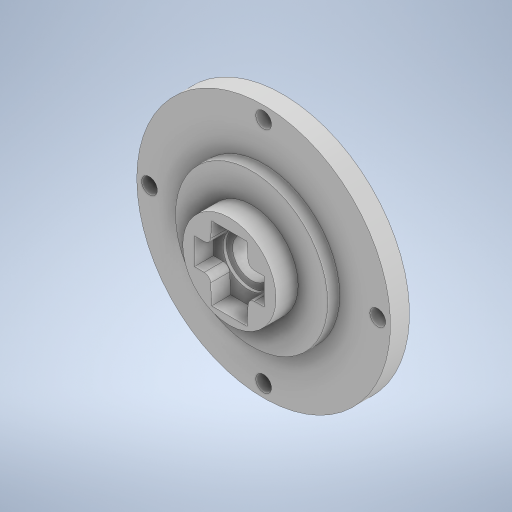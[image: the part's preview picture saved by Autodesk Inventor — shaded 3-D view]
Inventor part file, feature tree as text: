
AUTODESK INVENTOR PART (.ipt)
format: ipt  version: 2023.1 (Build 271208000, 208)  size: 600,576 bytes
history: native  units: mm
features: sketch x18, extrude x18, projected_geometry x7, fillet x2, other x1
ambient origin geometry x8: Origin, YZ Plane, XZ Plane, XY Plane, X Axis, Y Axis, Z Axis, Center Point
bodies: Body1 (feature_tree)
feature tree (46):
  other  "솔리드1"
  sketch  "스케치1"
  extrude  "돌출1"  Depth=5.0mm
  extrude  "돌출2"  Depth=1.9mm
  extrude  "돌출3"  Depth=16.5mm
  extrude  "돌출4"  Depth=29.0mm
  extrude  "돌출5"  Depth=1.0mm
  sketch  "스케치4"
  extrude  "돌출6"  Depth=1.0mm
  extrude  "돌출7"  Depth=1.0mm
  extrude  "돌출8"  Depth=1.0mm
  extrude  "돌출9"  Depth=20.0mm
  extrude  "돌출10"  Depth=20.0mm
  fillet  "모깎기1"  Radius=16.6mm
  sketch  "스케치11"
  extrude  "돌출11"  Depth=14.0mm
  sketch  "스케치14"
  extrude  "돌출12"  Depth=4.0mm
  extrude  "돌출13"  Depth=4.0mm
  extrude  "돌출14"  Depth=6.8mm
  extrude  "돌출15"  Depth=10.0mm
  fillet  "모깎기2"  Radius=4.7mm
  extrude  "돌출16"  Depth=20.0mm
  extrude  "돌출17"  Depth=10.0mm
  extrude  "돌출18"  Depth=2.2mm TaperAngle=0.0deg
  sketch  "스케치2"
  sketch  "스케치3"
  sketch  "스케치5"
  sketch  "스케치6"
  sketch  "스케치7"
  sketch  "스케치9"
  sketch  "스케치10"
  sketch  "스케치12"
  projected_geometry  "투영된 루프1"
  projected_geometry  "투영된 루프2"
  projected_geometry  "투영된 루프3"
  projected_geometry  "투영된 루프4"
  projected_geometry  "투영된 루프5"
  projected_geometry  "투영된 루프6"
  sketch  "스케치15"
  sketch  "스케치16"
  sketch  "스케치17"
  projected_geometry  "투영된 루프7"
  sketch  "스케치18"
  sketch  "스케치19"
  sketch  "스케치20"
